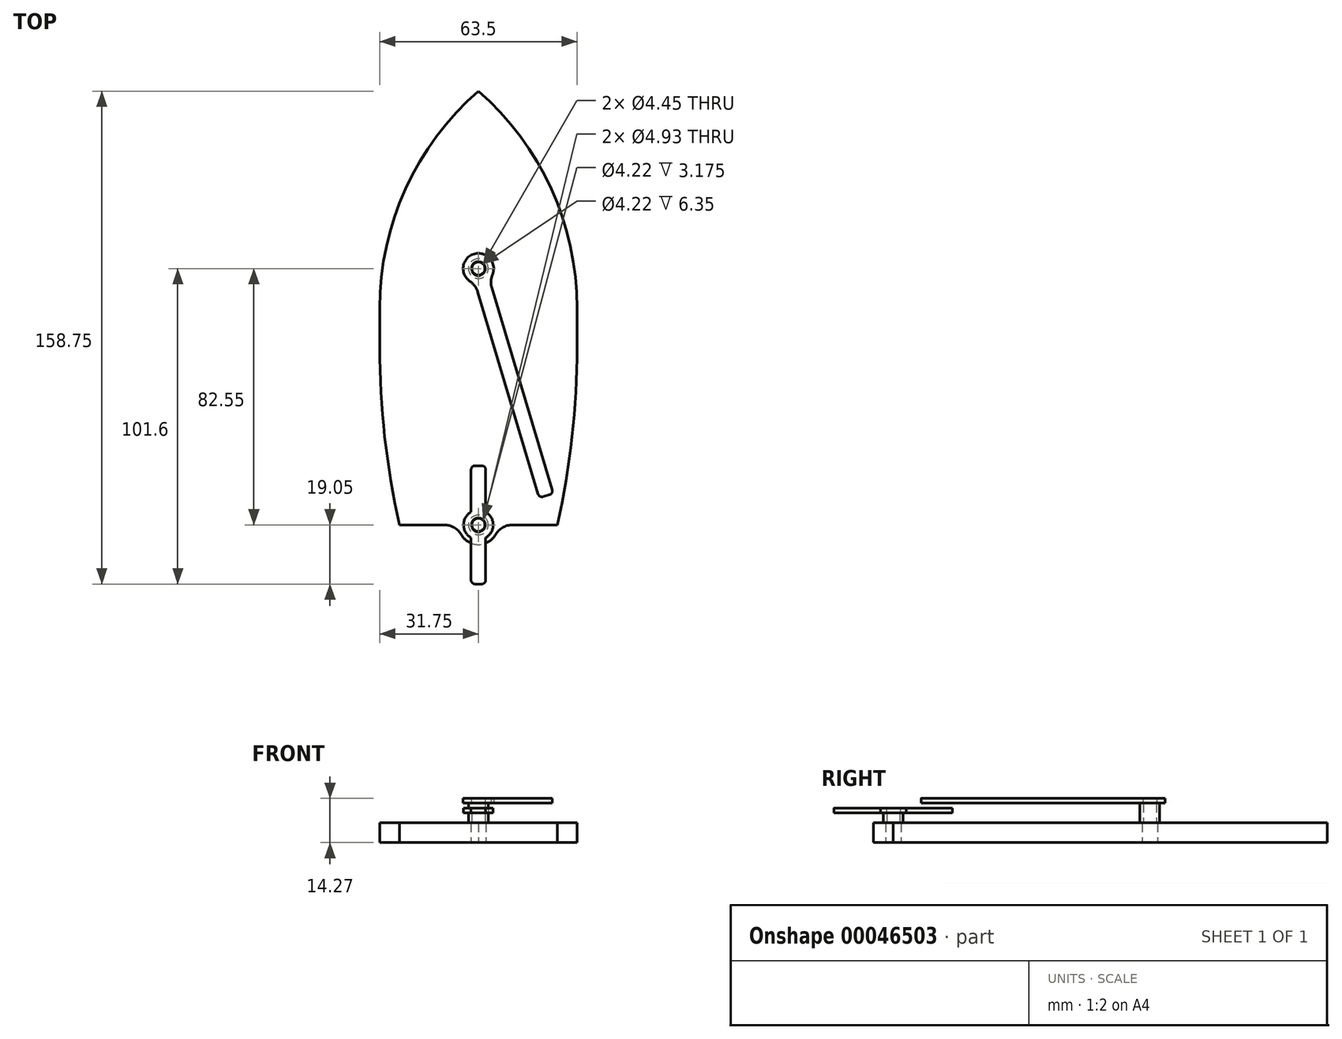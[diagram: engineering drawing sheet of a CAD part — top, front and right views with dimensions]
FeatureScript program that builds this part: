
annotation { "Feature Type Name" : "Feature", "Feature Type Description" : "" }
export const myFeature = defineFeature(function(context is Context, id is Id, definition is map)
    precondition{}
    {
        {
            var Q0;
            Q0=qCreatedBy(makeId("Top.planeOp"),FACE);
            var sketch = newSketch(context, id + "F0", { "sketchPlane" : qUnion([Q0])});
            skPoint(sketch, "E0.rect.middle", {"position": v(0, 0) * mm});
            skCircle(sketch, "E1", {"center": v(0, 12.7) * mm, "radius": 2.46 * mm});
            skPoint(sketch, "E2.endSnap0", {"position": v(-31.75, 0) * mm});
            skArc(sketch, "E3", {"start": v(-31.75, 0) * mm, "mid": v(-23.44, 38.36) * mm, "end": v(0, 69.85) * mm});
            skLineSegment(sketch, "E4", {"start": v(-31.75, 0) * mm, "end": v(-31.75, -12.7) * mm});
            skArc(sketch, "E5", {"start": v(-31.75, -12.7) * mm, "mid": v(-30.16, -41.45) * mm, "end": v(-25.4, -69.85) * mm});
            skLineSegment(sketch, "E6", {"start": v(-25.4, -69.85) * mm, "end": v(-11, -69.85) * mm});
            skArc(sketch, "E7.MirrorCS", {"start": v(31.75, 0) * mm, "mid": v(23.44, 38.36) * mm, "end": v(0, 69.85) * mm});
            skArc(sketch, "E8.MirrorCS", {"start": v(31.75, -12.7) * mm, "mid": v(30.16, -41.45) * mm, "end": v(25.4, -69.85) * mm});
            skLineSegment(sketch, "E9.MirrorCS", {"start": v(31.75, 0) * mm, "end": v(31.75, -12.7) * mm});
            skArc(sketch, "E10", {"start": v(-5.5, -73.03) * mm, "mid": v(0, -76.2) * mm, "end": v(5.5, -73.03) * mm});
            skCircle(sketch, "E11", {"center": v(0, -69.85) * mm, "radius": 2.46 * mm});
            skLineSegment(sketch, "E12.trimOffspring", {"start": v(11, -69.85) * mm, "end": v(25.4, -69.85) * mm});
            skLineSegment(sketch, "E13", {"start": v(-6.35, -69.85) * mm, "end": v(6.35, -69.85) * mm, "construction": true});
            skLineSegment(sketch, "E14", {"start": v(0, 0) * mm, "end": v(0, -85.3) * mm, "construction": true});
            skPoint(sketch, "E14.endSnap0", {"position": v(0, -76.2) * mm});
            skPoint(sketch, "E15.visualSharp", {"position": v(-6.35, -69.85) * mm});
            skArc(sketch, "E15.filletArc", {"start": v(-5.5, -73.03) * mm, "mid": v(-7.82, -70.7) * mm, "end": v(-11, -69.85) * mm});
            skPoint(sketch, "E16.visualSharp", {"position": v(6.35, -69.85) * mm});
            skArc(sketch, "E16.filletArc", {"start": v(11, -69.85) * mm, "mid": v(7.82, -70.7) * mm, "end": v(5.5, -73.03) * mm});
            skSolve(sketch);
        }
        {
            var Q0;
            Q0=makeQuery(id+"F0.imprint","IMPRINT",FACE,{"disambiguationData":[TD([[makeQuery(id+"F0.imprint","IMPRINT",EDGE,{"derivedFrom":sQuery(id+"F0.wireOp",EDGE,"E1")}),-1.0]])]});
            extrude(context, id + "F1", {"entities" : qUnion([Q0]), "depth" : 6.35 * mm});
        }
        {
            var Q0;
            Q0=makeQuery(id+"F1.opExtrude","CAP_FACE",FACE,{"disambiguationData":[OSD([sQuery(id+"F0.wireOp",EDGE,"E1"),sQuery(id+"F0.wireOp",EDGE,"E3"),sQuery(id+"F0.wireOp",EDGE,"E4"),sQuery(id+"F0.wireOp",EDGE,"E5"),sQuery(id+"F0.wireOp",EDGE,"E6"),sQuery(id+"F0.wireOp",EDGE,"E7.MirrorCS"),sQuery(id+"F0.wireOp",EDGE,"E8.MirrorCS"),sQuery(id+"F0.wireOp",EDGE,"E9.MirrorCS"),sQuery(id+"F0.wireOp",EDGE,"E10"),sQuery(id+"F0.wireOp",EDGE,"E11"),sQuery(id+"F0.wireOp",EDGE,"E12.trimOffspring"),sQuery(id+"F0.wireOp",EDGE,"E15.filletArc"),sQuery(id+"F0.wireOp",EDGE,"E16.filletArc")])],"isStart":false});
            var sketch = newSketch(context, id + "F2", { "sketchPlane" : qUnion([Q0])});
            skCircle(sketch, "E17", {"center": v(0, 12.7) * mm, "radius": 2.1 * mm});
            skCircle(sketch, "E18", {"center": v(0, 12.7) * mm, "radius": 3.18 * mm});
            skSolve(sketch);
        }
        {
            var Q0;
            Q0 = qSketchRegion(id + "F2", true);
            extrude(context, id + "F3", {"entities" : qUnion([Q0]), "depth" : 6.35 * mm});
        }
        {
            var Q0;
            Q0=makeQuery(id+"F1.opExtrude","CAP_FACE",FACE,{"disambiguationData":[OSD([sQuery(id+"F0.wireOp",EDGE,"E1"),sQuery(id+"F0.wireOp",EDGE,"E3"),sQuery(id+"F0.wireOp",EDGE,"E4"),sQuery(id+"F0.wireOp",EDGE,"E5"),sQuery(id+"F0.wireOp",EDGE,"E6"),sQuery(id+"F0.wireOp",EDGE,"E7.MirrorCS"),sQuery(id+"F0.wireOp",EDGE,"E8.MirrorCS"),sQuery(id+"F0.wireOp",EDGE,"E9.MirrorCS"),sQuery(id+"F0.wireOp",EDGE,"E10"),sQuery(id+"F0.wireOp",EDGE,"E11"),sQuery(id+"F0.wireOp",EDGE,"E12.trimOffspring"),sQuery(id+"F0.wireOp",EDGE,"E15.filletArc"),sQuery(id+"F0.wireOp",EDGE,"E16.filletArc")])],"isStart":false});
            var sketch = newSketch(context, id + "F4", { "sketchPlane" : qUnion([Q0])});
            skCircle(sketch, "E19", {"center": v(0, -69.85) * mm, "radius": 3.17 * mm});
            skCircle(sketch, "E20", {"center": v(0, -69.85) * mm, "radius": 2.1 * mm});
            skSolve(sketch);
        }
        {
            var Q0;
            Q0 = qSketchRegion(id + "F4", true);
            extrude(context, id + "F5", {"entities" : qUnion([Q0]), "depth" : 3.17 * mm});
        }
        {
            var Q0;
            Q0=makeQuery(id+"F3.opExtrude","CAP_FACE",FACE,{"disambiguationData":[OSD([sQuery(id+"F2.wireOp",EDGE,"E17"),sQuery(id+"F2.wireOp",EDGE,"E18")])],"isStart":false});
            var sketch = newSketch(context, id + "F6", { "sketchPlane" : qUnion([Q0])});
            skArc(sketch, "E21", {"start": v(4.53, 10.8) * mm, "mid": v(-1.4, 17.4) * mm, "end": v(-2.75, 8.63) * mm});
            skLineSegment(sketch, "E22", {"start": v(0, 12.7) * mm, "end": v(23.42, -65.72) * mm, "construction": true});
            skLineSegment(sketch, "E23.0", {"start": v(-0.22, 5.18) * mm, "end": v(19.23, -59.93) * mm});
            skLineSegment(sketch, "E24.0", {"start": v(4.3, 6.53) * mm, "end": v(23.75, -58.58) * mm});
            skCircle(sketch, "E25", {"center": v(0, 12.7) * mm, "radius": 2.22 * mm});
            skLineSegment(sketch, "E26", {"start": v(20.8, -60.78) * mm, "end": v(22.9, -60.16) * mm});
            skPoint(sketch, "E27.visualSharp", {"position": v(-1.03, 7.9) * mm});
            skArc(sketch, "E27.filletArc", {"start": v(-0.22, 5.18) * mm, "mid": v(-1.19, 7.12) * mm, "end": v(-2.75, 8.63) * mm});
            skPoint(sketch, "E28.visualSharp", {"position": v(3.5, 9.25) * mm});
            skArc(sketch, "E28.filletArc", {"start": v(4.53, 10.8) * mm, "mid": v(4.05, 8.69) * mm, "end": v(4.3, 6.53) * mm});
            skPoint(sketch, "E29.visualSharp", {"position": v(24.12, -59.8) * mm});
            skArc(sketch, "E29.filletArc", {"start": v(22.9, -60.16) * mm, "mid": v(23.65, -59.55) * mm, "end": v(23.75, -58.58) * mm});
            skPoint(sketch, "E30.visualSharp", {"position": v(19.59, -61.15) * mm});
            skArc(sketch, "E30.filletArc", {"start": v(19.23, -59.93) * mm, "mid": v(19.84, -60.68) * mm, "end": v(20.8, -60.78) * mm});
            skSolve(sketch);
        }
        {
            var Q0;
            Q0=makeQuery(id+"F6.imprint","IMPRINT",FACE,{"disambiguationData":[TD([[makeQuery(id+"F6.imprint","IMPRINT",EDGE,{"derivedFrom":sQuery(id+"F6.wireOp",EDGE,"E25")}),-1.0]])]});
            var Q1;
            Q1=makeQuery(id+"F6.imprint","IMPRINT",FACE,{"disambiguationData":[TD([[makeQuery(id+"F6.imprint","IMPRINT",EDGE,{"derivedFrom":sQuery(id+"F6.wireOp",EDGE,"E21")}),1.0]])]});
            extrude(context, id + "F7", {"entities" : qUnion([Q0, Q1]), "depth" : 1.57 * mm});
        }
        {
            var Q0;
            Q0=makeQuery(id+"F5.opExtrude","CAP_FACE",FACE,{"disambiguationData":[OSD([sQuery(id+"F4.wireOp",EDGE,"E19"),sQuery(id+"F4.wireOp",EDGE,"E20")])],"isStart":false});
            var sketch = newSketch(context, id + "F8", { "sketchPlane" : qUnion([Q0])});
            skCircle(sketch, "E31", {"center": v(0, -69.85) * mm, "radius": 2.22 * mm});
            skArc(sketch, "E32", {"start": v(-2.36, -65.71) * mm, "mid": v(-4.76, -69.85) * mm, "end": v(-2.36, -73.99) * mm});
            skLineSegment(sketch, "E33", {"start": v(0, -69.85) * mm, "end": v(0, -87.87) * mm, "construction": true});
            skLineSegment(sketch, "E34.0", {"start": v(-2.36, -52.07) * mm, "end": v(-2.36, -65.71) * mm});
            skLineSegment(sketch, "E35.0", {"start": v(2.36, -52.07) * mm, "end": v(2.36, -65.71) * mm});
            skLineSegment(sketch, "E36", {"start": v(-1.1, -88.9) * mm, "end": v(1.1, -88.9) * mm});
            skLineSegment(sketch, "E37.0", {"start": v(-1.1, -50.8) * mm, "end": v(1.1, -50.8) * mm});
            skLineSegment(sketch, "E38.trimOffspring", {"start": v(2.36, -73.99) * mm, "end": v(2.36, -87.63) * mm});
            skLineSegment(sketch, "E39.trimOffspring", {"start": v(-2.36, -73.99) * mm, "end": v(-2.36, -87.63) * mm});
            skArc(sketch, "E40.trimOffspring", {"start": v(2.36, -73.99) * mm, "mid": v(4.76, -69.85) * mm, "end": v(2.36, -65.71) * mm});
            skPoint(sketch, "E41.visualSharp", {"position": v(-2.36, -50.8) * mm});
            skArc(sketch, "E41.filletArc", {"start": v(-1.1, -50.8) * mm, "mid": v(-2, -51.17) * mm, "end": v(-2.36, -52.07) * mm});
            skPoint(sketch, "E42.visualSharp", {"position": v(2.36, -50.8) * mm});
            skArc(sketch, "E42.filletArc", {"start": v(2.36, -52.07) * mm, "mid": v(2, -51.17) * mm, "end": v(1.1, -50.8) * mm});
            skPoint(sketch, "E43.visualSharp", {"position": v(2.36, -88.9) * mm});
            skArc(sketch, "E43.filletArc", {"start": v(1.1, -88.9) * mm, "mid": v(2, -88.53) * mm, "end": v(2.36, -87.63) * mm});
            skPoint(sketch, "E44.visualSharp", {"position": v(-2.36, -88.9) * mm});
            skArc(sketch, "E44.filletArc", {"start": v(-2.36, -87.63) * mm, "mid": v(-2, -88.53) * mm, "end": v(-1.1, -88.9) * mm});
            skSolve(sketch);
        }
        {
            var Q0;
            Q0 = qSketchRegion(id + "F8", true);
            extrude(context, id + "F9", {"entities" : qUnion([Q0]), "depth" : 1.57 * mm});
        }
    });
